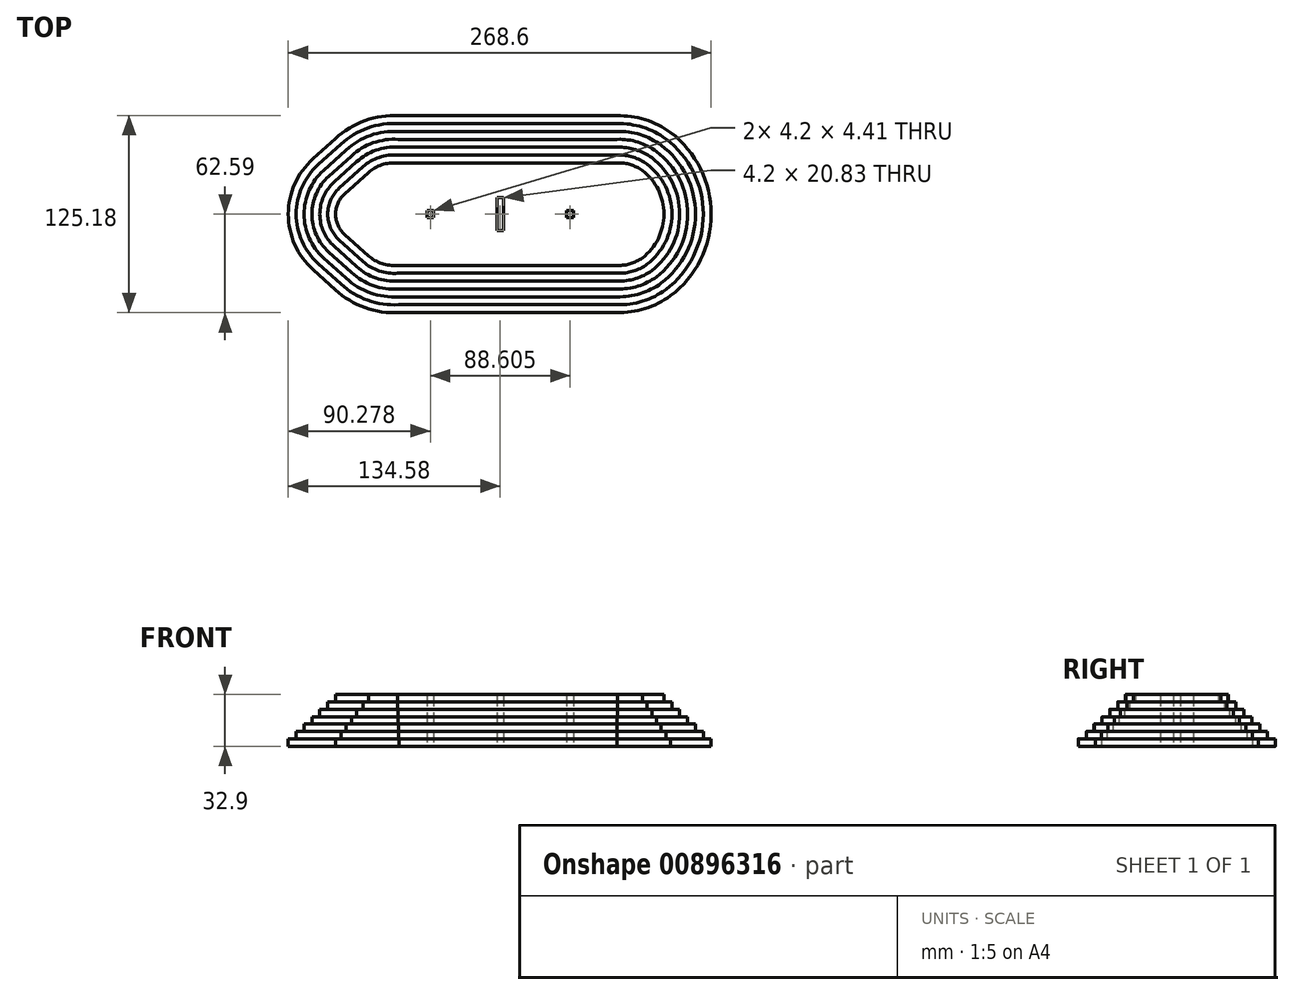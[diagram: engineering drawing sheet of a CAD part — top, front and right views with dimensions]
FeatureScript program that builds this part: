
annotation { "Feature Type Name" : "Feature", "Feature Type Description" : "" }
export const myFeature = defineFeature(function(context is Context, id is Id, definition is map)
    precondition{}
    {
        {
            var Q0;
            Q0=qCreatedBy(makeId("Top.planeOp"),FACE);
            var sketch = newSketch(context, id + "F0", { "sketchPlane" : qUnion([Q0])});
            skLineSegment(sketch, "E0.left", {"start": v(-75, 16.79) * mm, "end": v(-75, -16.79) * mm});
            skLineSegment(sketch, "E0.right", {"start": v(75, 17.5) * mm, "end": v(75, 0) * mm});
            skPoint(sketch, "E0.middle", {"position": v(0, 0) * mm});
            skPoint(sketch, "E1.endSnap0", {"position": v(-75, 0) * mm});
            skPoint(sketch, "E2", {"position": v(-3.7, 0) * mm});
            skLineSegment(sketch, "E3", {"start": v(-3.7, 0) * mm, "end": v(-92.3, 0) * mm});
            skLineSegment(sketch, "E4", {"start": v(-3.7, 0) * mm, "end": v(85.32, 0) * mm});
            skLineSegment(sketch, "E5", {"start": v(-92.51, 1.72) * mm, "end": v(-92.51, -1.72) * mm});
            skPoint(sketch, "E6.orphan", {"position": v(-94.42, 0) * mm});
            skPoint(sketch, "E7", {"position": v(-48, 0) * mm});
            skPoint(sketch, "E8", {"position": v(40.8, 0) * mm});
            skLineSegment(sketch, "E9.bottom", {"start": v(-50.1, 2.2) * mm, "end": v(-45.9, 2.2) * mm});
            skLineSegment(sketch, "E9.top", {"start": v(-50.1, -2.2) * mm, "end": v(-45.9, -2.2) * mm});
            skLineSegment(sketch, "E9.left", {"start": v(-50.1, 2.2) * mm, "end": v(-50.1, -2.2) * mm});
            skLineSegment(sketch, "E9.right", {"start": v(-45.9, 2.2) * mm, "end": v(-45.9, -2.2) * mm});
            skLineSegment(sketch, "E10", {"start": v(-3.7, 0) * mm, "end": v(-3.7, 17.5) * mm});
            skLineSegment(sketch, "E11.MirrorCS", {"start": v(38.5, 2.2) * mm, "end": v(38.5, -2.2) * mm});
            skLineSegment(sketch, "E12.MirrorCS", {"start": v(42.7, 2.2) * mm, "end": v(38.5, 2.2) * mm});
            skLineSegment(sketch, "E13.MirrorCS", {"start": v(42.7, 2.2) * mm, "end": v(42.7, -2.2) * mm});
            skLineSegment(sketch, "E14.MirrorCS", {"start": v(42.7, -2.2) * mm, "end": v(38.5, -2.2) * mm});
            skLineSegment(sketch, "E15.bottom", {"start": v(-5.8, 10.42) * mm, "end": v(-1.6, 10.42) * mm});
            skLineSegment(sketch, "E15.top", {"start": v(-5.8, -10.42) * mm, "end": v(-1.6, -10.42) * mm});
            skLineSegment(sketch, "E15.left", {"start": v(-5.8, 10.42) * mm, "end": v(-5.8, -10.42) * mm});
            skLineSegment(sketch, "E15.right", {"start": v(-1.6, 10.42) * mm, "end": v(-1.6, -10.42) * mm});
            skPoint(sketch, "E16.orphan", {"position": v(-75, 17.5) * mm});
            skPoint(sketch, "E17.orphan", {"position": v(-75, -17.5) * mm});
            skArc(sketch, "E18", {"start": v(-92.51, 1.72) * mm, "mid": v(-93.28, 0) * mm, "end": v(-92.51, -1.72) * mm});
            skArc(sketch, "E19.4", {"start": v(80.71, 19.7) * mm, "mid": v(80.68, 19.72) * mm, "end": v(80.64, 19.75) * mm});
            skArc(sketch, "E20.0", {"start": v(-68.99, 32.5) * mm, "mid": v(-78.84, 31.36) * mm, "end": v(-87.47, 26.46) * mm});
            skLineSegment(sketch, "E20.1", {"start": v(-87.47, 26.46) * mm, "end": v(-102.55, 12.87) * mm});
            skLineSegment(sketch, "E20.2", {"start": v(-68.99, 32.5) * mm, "end": v(70.9, 32.5) * mm});
            skArc(sketch, "E20.3", {"start": v(-102.55, 12.87) * mm, "mid": v(-108.28, 0) * mm, "end": v(-102.55, -12.87) * mm});
            skLineSegment(sketch, "E20.4", {"start": v(-102.55, -12.87) * mm, "end": v(-87.47, -26.46) * mm});
            skArc(sketch, "E20.5", {"start": v(-68.99, -32.5) * mm, "mid": v(-78.84, -31.36) * mm, "end": v(-87.47, -26.46) * mm});
            skArc(sketch, "E20.6", {"start": v(86.61, 27.78) * mm, "mid": v(79.15, 31.46) * mm, "end": v(70.9, 32.5) * mm});
            skArc(sketch, "E20.7", {"start": v(86.61, -27.78) * mm, "mid": v(100.32, 0) * mm, "end": v(86.61, 27.78) * mm});
            skArc(sketch, "E20.8", {"start": v(86.61, -27.78) * mm, "mid": v(79.15, -31.46) * mm, "end": v(70.9, -32.5) * mm});
            skLineSegment(sketch, "E20.9", {"start": v(-68.99, -32.5) * mm, "end": v(70.9, -32.5) * mm});
            skArc(sketch, "E21.0", {"start": v(-68.79, 37.5) * mm, "mid": v(-80.52, 36.07) * mm, "end": v(-90.79, 30.2) * mm});
            skLineSegment(sketch, "E21.1", {"start": v(-90.79, 30.2) * mm, "end": v(-105.9, 16.58) * mm});
            skLineSegment(sketch, "E21.2", {"start": v(-68.79, 37.5) * mm, "end": v(70.8, 37.5) * mm});
            skArc(sketch, "E21.3", {"start": v(-105.9, 16.58) * mm, "mid": v(-113.28, 0) * mm, "end": v(-105.9, -16.58) * mm});
            skLineSegment(sketch, "E21.4", {"start": v(-105.9, -16.58) * mm, "end": v(-90.79, -30.2) * mm});
            skArc(sketch, "E21.5", {"start": v(-68.79, -37.5) * mm, "mid": v(-80.52, -36.07) * mm, "end": v(-90.79, -30.2) * mm});
            skArc(sketch, "E21.6", {"start": v(89.6, 31.79) * mm, "mid": v(80.68, 36.22) * mm, "end": v(70.8, 37.5) * mm});
            skArc(sketch, "E21.7", {"start": v(89.6, -31.79) * mm, "mid": v(105.32, 0) * mm, "end": v(89.6, 31.79) * mm});
            skArc(sketch, "E21.8", {"start": v(89.6, -31.79) * mm, "mid": v(80.68, -36.22) * mm, "end": v(70.8, -37.5) * mm});
            skLineSegment(sketch, "E21.9", {"start": v(-68.79, -37.5) * mm, "end": v(70.8, -37.5) * mm});
            skArc(sketch, "E22.0", {"start": v(-68.6, 42.5) * mm, "mid": v(-82.67, 40.62) * mm, "end": v(-94.83, 33.29) * mm});
            skLineSegment(sketch, "E22.1", {"start": v(-94.83, 33.29) * mm, "end": v(-109.25, 20.3) * mm});
            skLineSegment(sketch, "E22.2", {"start": v(-68.6, 42.5) * mm, "end": v(70.7, 42.5) * mm});
            skArc(sketch, "E22.3", {"start": v(-109.25, 20.3) * mm, "mid": v(-118.28, 0) * mm, "end": v(-109.25, -20.3) * mm});
            skLineSegment(sketch, "E22.4", {"start": v(-109.25, -20.3) * mm, "end": v(-94.83, -33.29) * mm});
            skArc(sketch, "E22.5", {"start": v(-68.6, -42.5) * mm, "mid": v(-82.67, -40.62) * mm, "end": v(-94.83, -33.29) * mm});
            skArc(sketch, "E22.6", {"start": v(92.58, 35.8) * mm, "mid": v(82.2, 40.98) * mm, "end": v(70.7, 42.5) * mm});
            skArc(sketch, "E22.7", {"start": v(92.58, -35.8) * mm, "mid": v(110.32, 0) * mm, "end": v(92.58, 35.8) * mm});
            skArc(sketch, "E22.8", {"start": v(92.58, -35.8) * mm, "mid": v(82.2, -40.98) * mm, "end": v(70.7, -42.5) * mm});
            skLineSegment(sketch, "E22.9", {"start": v(-68.6, -42.5) * mm, "end": v(70.7, -42.5) * mm});
            skLineSegment(sketch, "E23.0", {"start": v(-68.79, 37.5) * mm, "end": v(70.7, 37.5) * mm});
            skArc(sketch, "E23.1", {"start": v(-68.79, 37.5) * mm, "mid": v(-80.95, 35.92) * mm, "end": v(-91.45, 29.6) * mm});
            skLineSegment(sketch, "E23.2", {"start": v(-91.45, 29.6) * mm, "end": v(-105.9, 16.58) * mm});
            skArc(sketch, "E24.0", {"start": v(-68.43, 47.5) * mm, "mid": v(-84.4, 45.3) * mm, "end": v(-98.2, 36.98) * mm});
            skLineSegment(sketch, "E24.1", {"start": v(-98.2, 36.98) * mm, "end": v(-112.6, 24.01) * mm});
            skLineSegment(sketch, "E24.2", {"start": v(-68.43, 47.5) * mm, "end": v(70.62, 47.5) * mm});
            skArc(sketch, "E24.3", {"start": v(-112.6, 24.01) * mm, "mid": v(-123.28, 0) * mm, "end": v(-112.6, -24.01) * mm});
            skLineSegment(sketch, "E24.4", {"start": v(-112.6, -24.01) * mm, "end": v(-98.2, -36.98) * mm});
            skArc(sketch, "E24.5", {"start": v(-68.43, -47.5) * mm, "mid": v(-84.4, -45.3) * mm, "end": v(-98.2, -36.98) * mm});
            skArc(sketch, "E24.6", {"start": v(95.57, 39.8) * mm, "mid": v(83.74, 45.74) * mm, "end": v(70.62, 47.5) * mm});
            skArc(sketch, "E24.7", {"start": v(95.57, -39.8) * mm, "mid": v(115.32, 0) * mm, "end": v(95.57, 39.8) * mm});
            skArc(sketch, "E24.8", {"start": v(95.57, -39.8) * mm, "mid": v(83.74, -45.74) * mm, "end": v(70.62, -47.5) * mm});
            skLineSegment(sketch, "E24.9", {"start": v(-68.43, -47.5) * mm, "end": v(70.62, -47.5) * mm});
            skLineSegment(sketch, "E25.0", {"start": v(-68.43, 42.5) * mm, "end": v(70.62, 42.5) * mm});
            skArc(sketch, "E26.0", {"start": v(-68.27, 52.5) * mm, "mid": v(-86.13, 50) * mm, "end": v(-101.57, 40.67) * mm});
            skLineSegment(sketch, "E26.1", {"start": v(-101.57, 40.67) * mm, "end": v(-115.94, 27.72) * mm});
            skLineSegment(sketch, "E26.2", {"start": v(-68.27, 52.5) * mm, "end": v(70.54, 52.5) * mm});
            skArc(sketch, "E26.3", {"start": v(-115.94, 27.72) * mm, "mid": v(-128.28, 0) * mm, "end": v(-115.94, -27.72) * mm});
            skLineSegment(sketch, "E26.4", {"start": v(-115.94, -27.72) * mm, "end": v(-101.57, -40.67) * mm});
            skArc(sketch, "E26.5", {"start": v(-68.27, -52.5) * mm, "mid": v(-86.13, -50) * mm, "end": v(-101.57, -40.67) * mm});
            skArc(sketch, "E26.6", {"start": v(98.56, 43.82) * mm, "mid": v(85.27, 50.5) * mm, "end": v(70.54, 52.5) * mm});
            skArc(sketch, "E26.7", {"start": v(98.56, -43.82) * mm, "mid": v(120.32, 0) * mm, "end": v(98.56, 43.82) * mm});
            skArc(sketch, "E26.8", {"start": v(98.56, -43.82) * mm, "mid": v(85.27, -50.5) * mm, "end": v(70.54, -52.5) * mm});
            skLineSegment(sketch, "E26.9", {"start": v(-68.27, -52.5) * mm, "end": v(70.54, -52.5) * mm});
            skLineSegment(sketch, "E27.0", {"start": v(-68.11, 57.5) * mm, "end": v(70.46, 57.5) * mm});
            skArc(sketch, "E27.1", {"start": v(101.55, 47.83) * mm, "mid": v(86.81, 55.26) * mm, "end": v(70.46, 57.5) * mm});
            skArc(sketch, "E27.2", {"start": v(-68.11, 57.5) * mm, "mid": v(-87.86, 54.7) * mm, "end": v(-104.94, 44.37) * mm});
            skArc(sketch, "E27.3", {"start": v(101.55, -47.83) * mm, "mid": v(125.32, 0) * mm, "end": v(101.55, 47.83) * mm});
            skArc(sketch, "E27.4", {"start": v(101.55, -47.83) * mm, "mid": v(86.81, -55.26) * mm, "end": v(70.46, -57.5) * mm});
            skLineSegment(sketch, "E27.5", {"start": v(-68.11, -57.5) * mm, "end": v(70.46, -57.5) * mm});
            skLineSegment(sketch, "E27.6", {"start": v(-104.94, 44.37) * mm, "end": v(-119.29, 31.44) * mm});
            skArc(sketch, "E27.7", {"start": v(-119.29, 31.44) * mm, "mid": v(-133.28, 0) * mm, "end": v(-119.29, -31.44) * mm});
            skLineSegment(sketch, "E27.8", {"start": v(-119.29, -31.44) * mm, "end": v(-104.94, -44.37) * mm});
            skArc(sketch, "E27.9", {"start": v(-68.11, -57.5) * mm, "mid": v(-87.86, -54.7) * mm, "end": v(-104.94, -44.37) * mm});
            skArc(sketch, "E28.0", {"start": v(-67.97, 62.5) * mm, "mid": v(-89.6, 59.38) * mm, "end": v(-108.3, 48.07) * mm});
            skLineSegment(sketch, "E28.1", {"start": v(-108.3, 48.07) * mm, "end": v(-122.63, 35.15) * mm});
            skLineSegment(sketch, "E28.2", {"start": v(-67.97, 62.5) * mm, "end": v(70.4, 62.5) * mm});
            skArc(sketch, "E28.3", {"start": v(-122.63, 35.15) * mm, "mid": v(-138.28, 0) * mm, "end": v(-122.63, -35.15) * mm});
            skLineSegment(sketch, "E28.4", {"start": v(-122.63, -35.15) * mm, "end": v(-108.3, -48.07) * mm});
            skArc(sketch, "E28.5", {"start": v(-67.97, -62.5) * mm, "mid": v(-89.6, -59.38) * mm, "end": v(-108.3, -48.07) * mm});
            skArc(sketch, "E28.6", {"start": v(104.54, 51.84) * mm, "mid": v(88.35, 60.02) * mm, "end": v(70.4, 62.5) * mm});
            skArc(sketch, "E28.7", {"start": v(104.54, -51.84) * mm, "mid": v(130.32, 0) * mm, "end": v(104.54, 51.84) * mm});
            skArc(sketch, "E28.8", {"start": v(104.54, -51.84) * mm, "mid": v(88.35, -60.02) * mm, "end": v(70.4, -62.5) * mm});
            skLineSegment(sketch, "E28.9", {"start": v(-67.97, -62.5) * mm, "end": v(70.4, -62.5) * mm});
            skLineSegment(sketch, "E29.bottom", {"start": v(-24.38, -315.24) * mm, "end": v(116.66, -315.24) * mm});
            skLineSegment(sketch, "E29.top", {"start": v(-24.38, -350.24) * mm, "end": v(116.66, -350.24) * mm});
            skLineSegment(sketch, "E29.left", {"start": v(-29.61, -315.95) * mm, "end": v(-29.61, -349.53) * mm});
            skLineSegment(sketch, "E29.right", {"start": v(120.39, -315.24) * mm, "end": v(120.39, -350.24) * mm});
            skPoint(sketch, "E29.middle", {"position": v(45.39, -332.74) * mm});
            skArc(sketch, "E30", {"start": v(123.05, -348.47) * mm, "mid": v(130.7, -332.74) * mm, "end": v(123.05, -317) * mm});
            skLineSegment(sketch, "E31", {"start": v(-32.15, -317.53) * mm, "end": v(-47.13, -331.02) * mm});
            skPoint(sketch, "E31.endSnap0", {"position": v(-29.61, -332.74) * mm});
            skLineSegment(sketch, "E32", {"start": v(-47.13, -334.46) * mm, "end": v(-32.15, -347.95) * mm});
            skPoint(sketch, "E33", {"position": v(41.69, -332.74) * mm});
            skLineSegment(sketch, "E34", {"start": v(41.69, -332.74) * mm, "end": v(-46.92, -332.74) * mm});
            skLineSegment(sketch, "E35", {"start": v(41.69, -332.74) * mm, "end": v(130.7, -332.74) * mm});
            skLineSegment(sketch, "E36", {"start": v(-47.13, -331.02) * mm, "end": v(-47.13, -334.46) * mm});
            skPoint(sketch, "E37.orphan", {"position": v(-49.04, -332.74) * mm});
            skPoint(sketch, "E38", {"position": v(-2.62, -332.74) * mm});
            skPoint(sketch, "E39", {"position": v(86.2, -332.74) * mm});
            skLineSegment(sketch, "E40.bottom", {"start": v(-4.72, -330.53) * mm, "end": v(-0.52, -330.53) * mm});
            skLineSegment(sketch, "E40.top", {"start": v(-4.72, -334.94) * mm, "end": v(-0.52, -334.94) * mm});
            skLineSegment(sketch, "E40.left", {"start": v(-4.72, -330.53) * mm, "end": v(-4.72, -334.94) * mm});
            skLineSegment(sketch, "E40.right", {"start": v(-0.52, -330.53) * mm, "end": v(-0.52, -334.94) * mm});
            skLineSegment(sketch, "E41", {"start": v(41.69, -332.74) * mm, "end": v(41.69, -315.24) * mm});
            skLineSegment(sketch, "E42.MirrorCS", {"start": v(83.89, -330.53) * mm, "end": v(83.89, -334.94) * mm});
            skLineSegment(sketch, "E43.MirrorCS", {"start": v(88.09, -330.53) * mm, "end": v(83.89, -330.53) * mm});
            skLineSegment(sketch, "E44.MirrorCS", {"start": v(88.09, -330.53) * mm, "end": v(88.09, -334.94) * mm});
            skLineSegment(sketch, "E45.MirrorCS", {"start": v(88.09, -334.94) * mm, "end": v(83.89, -334.94) * mm});
            skLineSegment(sketch, "E46.bottom", {"start": v(39.59, -322.32) * mm, "end": v(43.79, -322.32) * mm});
            skLineSegment(sketch, "E46.top", {"start": v(39.59, -343.15) * mm, "end": v(43.79, -343.15) * mm});
            skLineSegment(sketch, "E46.left", {"start": v(39.59, -322.32) * mm, "end": v(39.59, -343.15) * mm});
            skLineSegment(sketch, "E46.right", {"start": v(43.79, -322.32) * mm, "end": v(43.79, -343.15) * mm});
            skArc(sketch, "E47", {"start": v(-24.38, -315.24) * mm, "mid": v(-28.51, -315.55) * mm, "end": v(-32.15, -317.53) * mm});
            skPoint(sketch, "E48.orphan", {"position": v(-29.61, -315.24) * mm});
            skArc(sketch, "E49", {"start": v(123.05, -317) * mm, "mid": v(120, -315.58) * mm, "end": v(116.66, -315.24) * mm});
            skArc(sketch, "E50.MirrorCS", {"start": v(123.05, -348.47) * mm, "mid": v(120, -349.9) * mm, "end": v(116.66, -350.24) * mm});
            skArc(sketch, "E51.MirrorCS", {"start": v(-24.38, -350.24) * mm, "mid": v(-28.51, -349.92) * mm, "end": v(-32.15, -347.95) * mm});
            skPoint(sketch, "E52.orphan", {"position": v(-29.61, -350.24) * mm});
            skArc(sketch, "E53", {"start": v(-47.13, -331.02) * mm, "mid": v(-47.9, -332.74) * mm, "end": v(-47.13, -334.46) * mm});
            skArc(sketch, "E54.0", {"start": v(-24.08, -310.24) * mm, "mid": v(-30.14, -310.82) * mm, "end": v(-35.46, -313.77) * mm});
            skLineSegment(sketch, "E54.1", {"start": v(-24.08, -310.24) * mm, "end": v(118.13, -310.24) * mm});
            skLineSegment(sketch, "E54.2", {"start": v(-35.46, -313.77) * mm, "end": v(-50.47, -327.3) * mm});
            skArc(sketch, "E54.3", {"start": v(126.03, -312.99) * mm, "mid": v(122.28, -311.05) * mm, "end": v(118.13, -310.24) * mm});
            skArc(sketch, "E54.4", {"start": v(126.03, -352.49) * mm, "mid": v(135.7, -332.74) * mm, "end": v(126.03, -312.99) * mm});
            skArc(sketch, "E54.5", {"start": v(126.03, -352.49) * mm, "mid": v(122.28, -354.42) * mm, "end": v(118.13, -355.24) * mm});
            skArc(sketch, "E54.6", {"start": v(-50.47, -327.3) * mm, "mid": v(-52.9, -332.74) * mm, "end": v(-50.47, -338.17) * mm});
            skLineSegment(sketch, "E54.7", {"start": v(-50.47, -338.17) * mm, "end": v(-35.46, -351.7) * mm});
            skArc(sketch, "E54.8", {"start": v(-24.08, -355.24) * mm, "mid": v(-30.14, -354.66) * mm, "end": v(-35.46, -351.7) * mm});
            skLineSegment(sketch, "E54.9", {"start": v(-24.08, -355.24) * mm, "end": v(118.13, -355.24) * mm});
            skArc(sketch, "E55.0", {"start": v(-23.83, -305.24) * mm, "mid": v(-31.79, -306.1) * mm, "end": v(-38.77, -310.02) * mm});
            skLineSegment(sketch, "E55.1", {"start": v(-38.77, -310.02) * mm, "end": v(-53.82, -323.59) * mm});
            skArc(sketch, "E55.3", {"start": v(-53.82, -323.59) * mm, "mid": v(-57.9, -332.74) * mm, "end": v(-53.82, -341.89) * mm});
            skLineSegment(sketch, "E55.4", {"start": v(-53.82, -341.89) * mm, "end": v(-38.77, -355.45) * mm});
            skArc(sketch, "E55.5", {"start": v(-23.83, -360.24) * mm, "mid": v(-31.79, -359.38) * mm, "end": v(-38.77, -355.45) * mm});
            skArc(sketch, "E55.6", {"start": v(129.01, -308.97) * mm, "mid": v(123.9, -306.33) * mm, "end": v(118.26, -305.24) * mm});
            skArc(sketch, "E55.7", {"start": v(129.01, -356.5) * mm, "mid": v(140.7, -332.74) * mm, "end": v(129.01, -308.97) * mm});
            skArc(sketch, "E55.8", {"start": v(129.01, -356.5) * mm, "mid": v(123.9, -359.15) * mm, "end": v(118.26, -360.24) * mm});
            skLineSegment(sketch, "E55.9", {"start": v(-23.83, -360.24) * mm, "end": v(118.26, -360.24) * mm});
            skLineSegment(sketch, "E56.0", {"start": v(-24.08, -310.24) * mm, "end": v(116.15, -310.24) * mm});
            skArc(sketch, "E56.5", {"start": v(126.03, -352.49) * mm, "mid": v(135.7, -332.78) * mm, "end": v(126.1, -313.04) * mm});
            skArc(sketch, "E57.0", {"start": v(-23.6, -300.24) * mm, "mid": v(-33.46, -301.38) * mm, "end": v(-42.08, -306.28) * mm});
            skLineSegment(sketch, "E57.1", {"start": v(-42.08, -306.28) * mm, "end": v(-57.17, -319.87) * mm});
            skArc(sketch, "E57.3", {"start": v(-57.17, -319.87) * mm, "mid": v(-62.9, -332.74) * mm, "end": v(-57.17, -345.6) * mm});
            skLineSegment(sketch, "E57.4", {"start": v(-57.17, -345.6) * mm, "end": v(-42.08, -359.2) * mm});
            skArc(sketch, "E57.5", {"start": v(-23.6, -365.24) * mm, "mid": v(-33.46, -364.1) * mm, "end": v(-42.08, -359.2) * mm});
            skArc(sketch, "E57.6", {"start": v(132, -304.96) * mm, "mid": v(124.54, -301.28) * mm, "end": v(116.28, -300.24) * mm});
            skArc(sketch, "E57.7", {"start": v(132, -360.52) * mm, "mid": v(145.7, -332.74) * mm, "end": v(132, -304.96) * mm});
            skArc(sketch, "E57.8", {"start": v(132, -360.52) * mm, "mid": v(124.54, -364.2) * mm, "end": v(116.28, -365.24) * mm});
            skLineSegment(sketch, "E57.9", {"start": v(-23.6, -365.24) * mm, "end": v(116.28, -365.24) * mm});
            skArc(sketch, "E58.0", {"start": v(-23.4, -295.24) * mm, "mid": v(-35.14, -296.67) * mm, "end": v(-45.4, -302.54) * mm});
            skLineSegment(sketch, "E58.1", {"start": v(-45.4, -302.54) * mm, "end": v(-60.51, -316.16) * mm});
            skArc(sketch, "E58.3", {"start": v(-60.51, -316.16) * mm, "mid": v(-67.9, -332.74) * mm, "end": v(-60.51, -349.32) * mm});
            skLineSegment(sketch, "E58.4", {"start": v(-60.51, -349.32) * mm, "end": v(-45.4, -362.94) * mm});
            skArc(sketch, "E58.5", {"start": v(-23.4, -370.24) * mm, "mid": v(-35.14, -368.8) * mm, "end": v(-45.4, -362.94) * mm});
            skArc(sketch, "E58.6", {"start": v(134.98, -300.95) * mm, "mid": v(126.06, -296.51) * mm, "end": v(116.18, -295.24) * mm});
            skArc(sketch, "E58.7", {"start": v(134.98, -364.53) * mm, "mid": v(150.7, -332.74) * mm, "end": v(134.98, -300.95) * mm});
            skArc(sketch, "E58.8", {"start": v(134.98, -364.53) * mm, "mid": v(126.06, -368.96) * mm, "end": v(116.18, -370.24) * mm});
            skLineSegment(sketch, "E58.9", {"start": v(-23.4, -370.24) * mm, "end": v(116.18, -370.24) * mm});
            skArc(sketch, "E59.0", {"start": v(-23.22, -290.24) * mm, "mid": v(-37.28, -292.12) * mm, "end": v(-49.44, -299.45) * mm});
            skLineSegment(sketch, "E59.1", {"start": v(-49.44, -299.45) * mm, "end": v(-63.86, -312.44) * mm});
            skLineSegment(sketch, "E59.2", {"start": v(-23.22, -290.24) * mm, "end": v(116.09, -290.24) * mm});
            skArc(sketch, "E59.3", {"start": v(-63.86, -312.44) * mm, "mid": v(-72.9, -332.74) * mm, "end": v(-63.86, -353.03) * mm});
            skLineSegment(sketch, "E59.4", {"start": v(-63.86, -353.03) * mm, "end": v(-49.44, -366.03) * mm});
            skArc(sketch, "E59.5", {"start": v(-23.22, -375.24) * mm, "mid": v(-37.28, -373.35) * mm, "end": v(-49.44, -366.03) * mm});
            skArc(sketch, "E59.6", {"start": v(137.97, -296.94) * mm, "mid": v(127.6, -291.75) * mm, "end": v(116.09, -290.24) * mm});
            skArc(sketch, "E59.7", {"start": v(137.97, -368.54) * mm, "mid": v(155.7, -332.74) * mm, "end": v(137.97, -296.94) * mm});
            skArc(sketch, "E59.8", {"start": v(137.97, -368.54) * mm, "mid": v(127.6, -373.72) * mm, "end": v(116.09, -375.24) * mm});
            skLineSegment(sketch, "E59.9", {"start": v(-23.22, -375.24) * mm, "end": v(116.09, -375.24) * mm});
            skArc(sketch, "E60.1", {"start": v(-23.4, -295.24) * mm, "mid": v(-35.56, -296.82) * mm, "end": v(-46.07, -303.14) * mm});
            skLineSegment(sketch, "E60.2", {"start": v(-46.07, -303.14) * mm, "end": v(-60.51, -316.16) * mm});
            skArc(sketch, "E61.0", {"start": v(-23.04, -285.24) * mm, "mid": v(-39.01, -287.43) * mm, "end": v(-52.81, -295.76) * mm});
            skLineSegment(sketch, "E61.1", {"start": v(-52.81, -295.76) * mm, "end": v(-67.2, -308.73) * mm});
            skArc(sketch, "E61.3", {"start": v(-67.2, -308.73) * mm, "mid": v(-77.9, -332.74) * mm, "end": v(-67.2, -356.75) * mm});
            skLineSegment(sketch, "E61.4", {"start": v(-67.2, -356.75) * mm, "end": v(-52.81, -369.72) * mm});
            skArc(sketch, "E61.5", {"start": v(-23.04, -380.24) * mm, "mid": v(-39.01, -378.05) * mm, "end": v(-52.81, -369.72) * mm});
            skArc(sketch, "E61.6", {"start": v(140.96, -292.93) * mm, "mid": v(129.12, -287) * mm, "end": v(116, -285.24) * mm});
            skArc(sketch, "E61.7", {"start": v(140.96, -372.55) * mm, "mid": v(160.7, -332.74) * mm, "end": v(140.96, -292.93) * mm});
            skArc(sketch, "E61.8", {"start": v(140.96, -372.55) * mm, "mid": v(129.12, -378.48) * mm, "end": v(116, -380.24) * mm});
            skLineSegment(sketch, "E61.9", {"start": v(-23.04, -380.24) * mm, "end": v(116, -380.24) * mm});
            skLineSegment(sketch, "E62.0", {"start": v(-23.04, -290.24) * mm, "end": v(116, -290.24) * mm});
            skArc(sketch, "E63.0", {"start": v(-22.88, -280.24) * mm, "mid": v(-40.74, -282.74) * mm, "end": v(-56.18, -292.06) * mm});
            skLineSegment(sketch, "E63.1", {"start": v(-56.18, -292.06) * mm, "end": v(-70.55, -305.01) * mm});
            skArc(sketch, "E63.3", {"start": v(-70.55, -305.01) * mm, "mid": v(-82.9, -332.74) * mm, "end": v(-70.55, -360.46) * mm});
            skLineSegment(sketch, "E63.4", {"start": v(-70.55, -360.46) * mm, "end": v(-56.18, -373.41) * mm});
            skArc(sketch, "E63.5", {"start": v(-22.88, -385.24) * mm, "mid": v(-40.74, -382.74) * mm, "end": v(-56.18, -373.41) * mm});
            skArc(sketch, "E63.6", {"start": v(143.94, -288.92) * mm, "mid": v(130.66, -282.23) * mm, "end": v(115.92, -280.24) * mm});
            skArc(sketch, "E63.7", {"start": v(143.94, -376.56) * mm, "mid": v(165.7, -332.74) * mm, "end": v(143.94, -288.92) * mm});
            skArc(sketch, "E63.8", {"start": v(143.94, -376.56) * mm, "mid": v(130.66, -383.24) * mm, "end": v(115.92, -385.24) * mm});
            skLineSegment(sketch, "E63.9", {"start": v(-22.88, -385.24) * mm, "end": v(115.92, -385.24) * mm});
            skArc(sketch, "E64.1", {"start": v(146.93, -284.91) * mm, "mid": v(132.2, -277.48) * mm, "end": v(115.85, -275.24) * mm});
            skArc(sketch, "E64.2", {"start": v(-22.73, -275.24) * mm, "mid": v(-42.48, -278.05) * mm, "end": v(-59.55, -288.37) * mm});
            skArc(sketch, "E64.3", {"start": v(146.93, -380.56) * mm, "mid": v(170.7, -332.74) * mm, "end": v(146.93, -284.91) * mm});
            skArc(sketch, "E64.4", {"start": v(146.93, -380.56) * mm, "mid": v(132.2, -388) * mm, "end": v(115.85, -390.24) * mm});
            skLineSegment(sketch, "E64.5", {"start": v(-22.73, -390.24) * mm, "end": v(115.85, -390.24) * mm});
            skLineSegment(sketch, "E64.6", {"start": v(-59.55, -288.37) * mm, "end": v(-73.9, -301.3) * mm});
            skArc(sketch, "E64.7", {"start": v(-73.9, -301.3) * mm, "mid": v(-87.9, -332.74) * mm, "end": v(-73.9, -364.18) * mm});
            skLineSegment(sketch, "E64.8", {"start": v(-73.9, -364.18) * mm, "end": v(-59.55, -377.1) * mm});
            skArc(sketch, "E64.9", {"start": v(-22.73, -390.24) * mm, "mid": v(-42.48, -387.43) * mm, "end": v(-59.55, -377.1) * mm});
            skArc(sketch, "E65.0", {"start": v(-22.58, -270.24) * mm, "mid": v(-44.21, -273.36) * mm, "end": v(-62.92, -284.67) * mm});
            skLineSegment(sketch, "E65.1", {"start": v(-62.92, -284.67) * mm, "end": v(-77.25, -297.58) * mm});
            skArc(sketch, "E65.3", {"start": v(-77.25, -297.58) * mm, "mid": v(-92.9, -332.74) * mm, "end": v(-77.25, -367.9) * mm});
            skLineSegment(sketch, "E65.4", {"start": v(-77.25, -367.9) * mm, "end": v(-62.92, -380.8) * mm});
            skArc(sketch, "E65.5", {"start": v(-22.58, -395.24) * mm, "mid": v(-44.21, -392.12) * mm, "end": v(-62.92, -380.8) * mm});
            skArc(sketch, "E65.6", {"start": v(149.92, -280.9) * mm, "mid": v(133.74, -272.72) * mm, "end": v(115.78, -270.24) * mm});
            skArc(sketch, "E65.7", {"start": v(149.92, -384.57) * mm, "mid": v(175.7, -332.74) * mm, "end": v(149.92, -280.9) * mm});
            skArc(sketch, "E65.8", {"start": v(149.92, -384.57) * mm, "mid": v(133.74, -392.76) * mm, "end": v(115.78, -395.24) * mm});
            skLineSegment(sketch, "E65.9", {"start": v(-22.58, -395.24) * mm, "end": v(115.78, -395.24) * mm});
            skLineSegment(sketch, "E66.trimOffspring", {"start": v(75, -17.04) * mm, "end": v(75, -17.5) * mm});
            skPoint(sketch, "E67.MirrorCS.end.orphan", {"position": v(71.28, -17.5) * mm});
            skPoint(sketch, "E68.orphan", {"position": v(77.67, -15.73) * mm});
            skPoint(sketch, "E69.orphan", {"position": v(77.67, 15.73) * mm});
            skPoint(sketch, "E70.end.orphan", {"position": v(71.28, 17.5) * mm});
            skSolve(sketch);
        }
        {
            var Q0;
            Q0=makeQuery(id+"F0.imprint","IMPRINT",FACE,{"disambiguationData":[TD([[makeQuery(id+"F0.imprint","IMPRINT",EDGE,{"derivedFrom":sQuery(id+"F0.wireOp",EDGE,"E27.0")}),1.0]])]});
            extrude(context, id + "F1", {"entities" : qUnion([Q0]), "depth" : 4.7 * mm, "offsetDistance" : 25 * mm});
        }
        {
            var Q0;
            Q0=makeQuery(id+"F0.imprint","IMPRINT",FACE,{"disambiguationData":[TD([[makeQuery(id+"F0.imprint","IMPRINT",EDGE,{"derivedFrom":sQuery(id+"F0.wireOp",EDGE,"E26.0")}),-1.0]])]});
            extrude(context, id + "F2", {"entities" : qUnion([Q0]), "operationType" : NewBodyOperationType.ADD, "depth" : (4.7 + 4.7) * mm, "offsetDistance" : 25 * mm});
        }
        {
            var Q0;
            Q0=makeQuery(id+"F0.imprint","IMPRINT",FACE,{"disambiguationData":[TD([[makeQuery(id+"F0.imprint","IMPRINT",EDGE,{"derivedFrom":sQuery(id+"F0.wireOp",EDGE,"E24.0")}),-1.0]])]});
            extrude(context, id + "F3", {"entities" : qUnion([Q0]), "operationType" : NewBodyOperationType.ADD, "depth" : (4.7 + 4.7 + 4.7) * mm, "offsetDistance" : 25 * mm});
        }
        {
            var Q0;
            {var subQ1=sQuery(id+"F0.wireOp",EDGE,"E22.0");Q0=makeQuery(id+"F0.imprint","IMPRINT",FACE,{"disambiguationData":[TD([[makeQuery(id+"F0.imprint","IMPRINT",EDGE,{"derivedFrom":subQ1}),-1.0]])]});}
            extrude(context, id + "F4", {"entities" : qUnion([Q0]), "operationType" : NewBodyOperationType.ADD, "depth" : (4.7 + 4.7 + 4.7 + 4.7) * mm, "offsetDistance" : 25 * mm});
        }
        {
            var Q0;
            Q0=makeQuery(id+"F0.imprint","IMPRINT",FACE,{"disambiguationData":[TD([[makeQuery(id+"F0.imprint","IMPRINT",EDGE,{"derivedFrom":sQuery(id+"F0.wireOp",EDGE,"E21.2")}),1.0]])]});
            extrude(context, id + "F5", {"entities" : qUnion([Q0]), "operationType" : NewBodyOperationType.ADD, "depth" : (4.7 + 4.7 + 4.7 + 4.7 + 4.7) * mm, "offsetDistance" : 25 * mm});
        }
        {
            var Q0;
            Q0=makeQuery(id+"F0.imprint","IMPRINT",FACE,{"disambiguationData":[TD([[makeQuery(id+"F0.imprint","IMPRINT",EDGE,{"derivedFrom":sQuery(id+"F0.wireOp",EDGE,"E20.0")}),-1.0]])]});
            extrude(context, id + "F6", {"entities" : qUnion([Q0]), "operationType" : NewBodyOperationType.ADD, "depth" : (4.7 + 4.7 + 4.7 + 4.7 + 4.7 + 4.7) * mm, "offsetDistance" : 25 * mm});
        }
        {
            var Q0;
            Q0=makeQuery(id+"F0.imprint","IMPRINT",FACE,{"disambiguationData":[TD([[makeQuery(id+"F0.imprint","IMPRINT",EDGE,{"derivedFrom":sQuery(id+"F0.wireOp",EDGE,"E5")}),1.0]])]});
            var Q1;
            Q1=makeQuery(id+"F0.imprint","IMPRINT",FACE,{"disambiguationData":[TD([[makeQuery(id+"F0.imprint","IMPRINT",EDGE,{"derivedFrom":sQuery(id+"F0.wireOp",EDGE,"E5")}),-1.0]])]});
            extrude(context, id + "F7", {"entities" : qUnion([Q0, Q1]), "operationType" : NewBodyOperationType.ADD, "depth" : (4.7 * 7) * mm, "offsetDistance" : 25 * mm});
        }
    });
